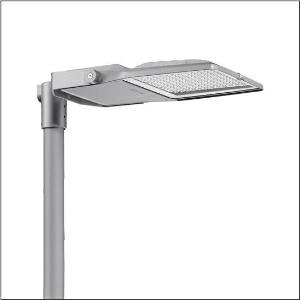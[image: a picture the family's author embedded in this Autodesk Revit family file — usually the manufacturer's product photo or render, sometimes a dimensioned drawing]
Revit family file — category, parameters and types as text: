
# Revit family: floodlight_fl_21_iq_midi___pl33t_5xa7781e4f3a_bb4e
name_source: partatom
category: Lighting Fixtures
units: mm (PartAtom-declared; Revit-internal decimal feet)

## family parameters
Cut with Voids When Loaded = No
Host = Face
Light Source = No
Part Type = Normal
Room Calculation Point = No
Round Connector Dimension = Use Diameter
Shared = No

## types (1)
- --- (1 x LED, 27690 lm, 208.1 W, 4000K)
    Apparent Load = 208 VA
    CIE Flux Codes = 26 75 99 100 100
    Color Rendering = 70
    Color Temperature = 4000K
    Default Elevation = 1800 mm
    Description = Floodlight FL 21 iQ midi, floodlight, primary light control with lens, of PMMA, primary optical cover: protective disc, of toughened safety glass, transparent, light distribution: PL33T, light emission: direct distribution, installation type: surface-mounted, LED, High Power LED, rated luminous flux: 27.690lm, luminous efficacy: 133lm/W, light colour: 740, colour temperature: 4000K, control gear: ECG iQ, control: optimised constant luminous flux control (CLO 2.0), Desk-Remote (wireless, voltage-free reading and setting of iQ features in the workshop via application-optimized NFC function/RFID function), Light-Fading, Smart-Wire, Night-Set, Lumen-Switch, Temp-Guard, Auto-Match, with terminal, 6-pole, mains connection: 220..240V, AC, 50/60Hz, start of lifetime: 208W, end of service life: 227W, reduction: 90W, luminaire housing, of diecast aluminium, powder-coated, Siteco® metallic grey (DB 702S), corrosivity category C5 mid according to DIN EN ISO 12944, sealing non-destructively replaceable, please order mast flange separately, mast bracket, of steel, galvanised, powder-coated, Siteco® metallic grey (DB 702S), protection rating (complete): IP66, insulation class (complete): insulation class II (safety insulation), certification: CE, protection symbol: D, impact resistance: IK08, permissible operating ambient temperature: -40..+40°C, permissible operating ambient temperature for outdoor applications: -40..+50°C, standard: DIN EN 12944, LABS conformity tested according to VDMA 24364:2018-05, packaging unit: 1 piece

Light Distribution: PL33T
    Height = 76 mm
    Lamp = 1 x LED
    Lamp Light Flux = 27690 lm
    Lamp Power = 208.1 W
    Lamp count = 1
    Length = 657 mm
    Luminous efficacy = 133 lm/W
    Manufacturer = Siteco
    ModVariant = No
    Model = 5XA7781E4F3A
    Number of Poles = 1
    OnlyDefault = Yes
    Power Factor = 1
    Product Name = Floodlight FL 21 iQ midi | PL33T
    Product group = floodlight | pylon annexe
    ProductGroupID = 6200
    Protection Class = Protection class II
    Protection Degree = IP 66
    RLX_Detail_Level = 1
    RLX_Emergency_Light_Flux = 0 lm
    RLX_Emergency_Type = 0
    RLX_Emergency_Type_DB = No
    RlxData = <blob elided: 153297 chars, md5=fa3e1ca9>
    Socket = socket
    Standby Power = 0 W
    System Light Flux = 27690 lm
    System Power = 208 W
    Type Comments = factory setting: luminous flux: 100 % | dim-lin: 254 | 710 mA
    Type Image = l_1007123.jpg
    URL = http://relux.com
    VarID = @adj_052229
    Voltage = 0 V
    Weight = 0.00 kg
    Width = 442 mm

## geometry (parser evidence)
native form markers: Blend x4, Sweep x15
no freeform markers — native parametric forms only
